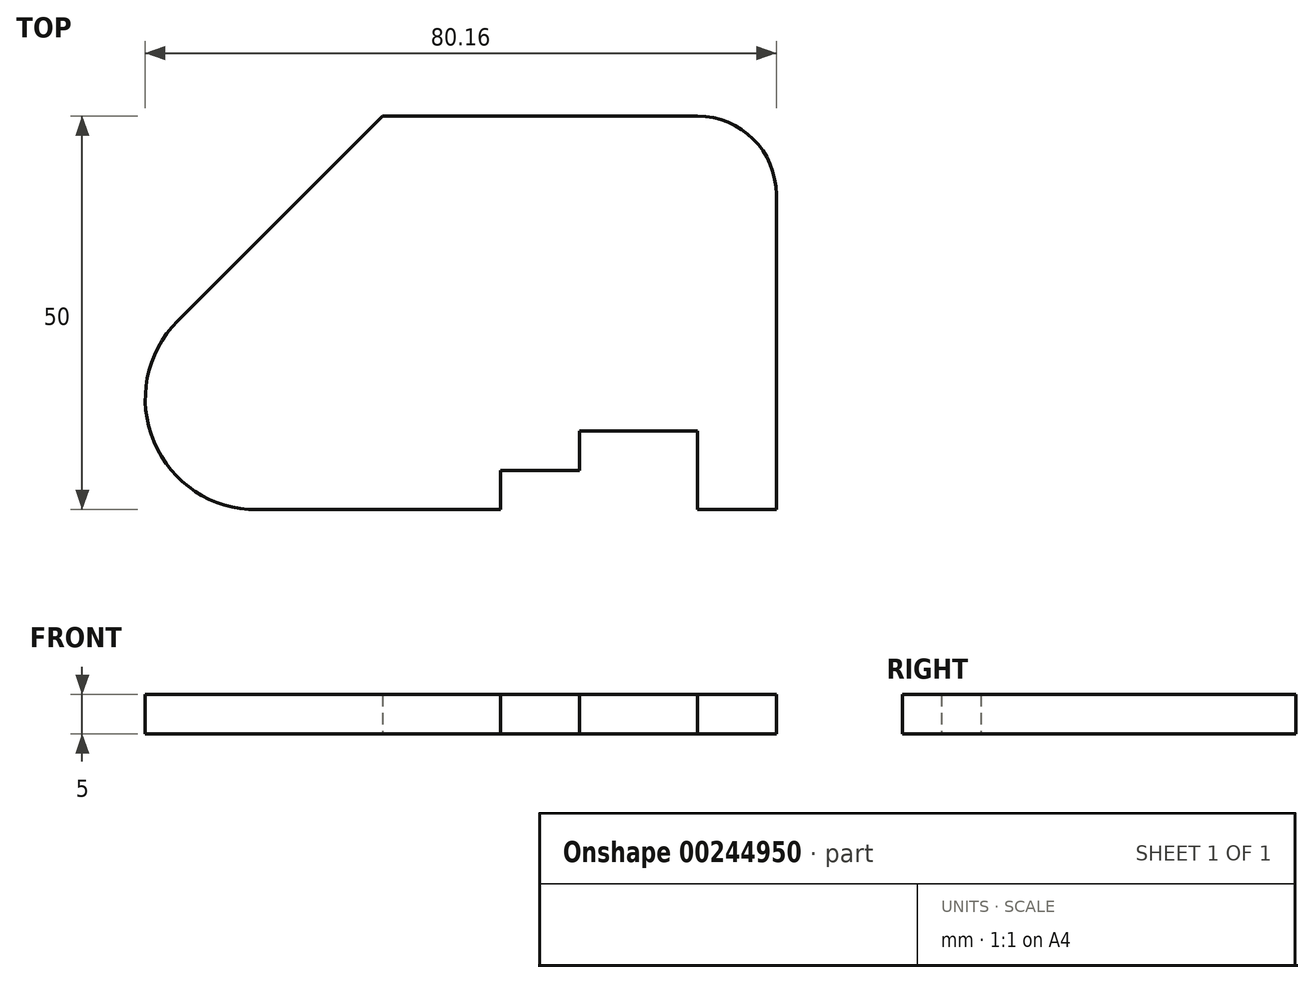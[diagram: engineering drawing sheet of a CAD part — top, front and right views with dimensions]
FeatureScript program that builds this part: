
annotation { "Feature Type Name" : "Feature", "Feature Type Description" : "" }
export const myFeature = defineFeature(function(context is Context, id is Id, definition is map)
    precondition{}
    {
        {
            var Q0;
            Q0=qCreatedBy(makeId("Top.planeOp"),FACE);
            var sketch = newSketch(context, id + "F0", { "sketchPlane" : qUnion([Q0])});
            skLineSegment(sketch, "E0", {"start": v(-23.95, 26.05) * mm, "end": v(16.05, 26.05) * mm});
            skLineSegment(sketch, "E1", {"start": v(26.05, 16.05) * mm, "end": v(26.05, -23.95) * mm});
            skLineSegment(sketch, "E2", {"start": v(26.05, -23.95) * mm, "end": v(16.05, -23.95) * mm});
            skLineSegment(sketch, "E3", {"start": v(16.05, -23.95) * mm, "end": v(16.05, -13.95) * mm});
            skLineSegment(sketch, "E4", {"start": v(16.05, -13.95) * mm, "end": v(1.05, -13.95) * mm});
            skLineSegment(sketch, "E5", {"start": v(1.05, -13.95) * mm, "end": v(1.05, -18.95) * mm});
            skLineSegment(sketch, "E6", {"start": v(1.05, -18.95) * mm, "end": v(-8.95, -18.95) * mm});
            skLineSegment(sketch, "E7", {"start": v(-8.95, -18.95) * mm, "end": v(-8.95, -23.95) * mm});
            skLineSegment(sketch, "E8", {"start": v(-8.95, -23.95) * mm, "end": v(-39.95, -23.95) * mm});
            skLineSegment(sketch, "E9", {"start": v(-50, 0) * mm, "end": v(-23.95, 26.05) * mm});
            skPoint(sketch, "E10.visualSharp", {"position": v(26.05, 26.05) * mm});
            skArc(sketch, "E10.filletArc", {"start": v(26.05, 16.05) * mm, "mid": v(23.12, 23.12) * mm, "end": v(16.05, 26.05) * mm});
            skArc(sketch, "E11", {"start": v(-50, 0) * mm, "mid": v(-53.02, -15.35) * mm, "end": v(-39.95, -23.95) * mm});
            skSolve(sketch);
        }
        {
            var Q0;
            Q0 = qSketchRegion(id + "F0", true);
            extrude(context, id + "F1", {"entities" : qUnion([Q0]), "depth" : 5 * mm});
        }
    });
